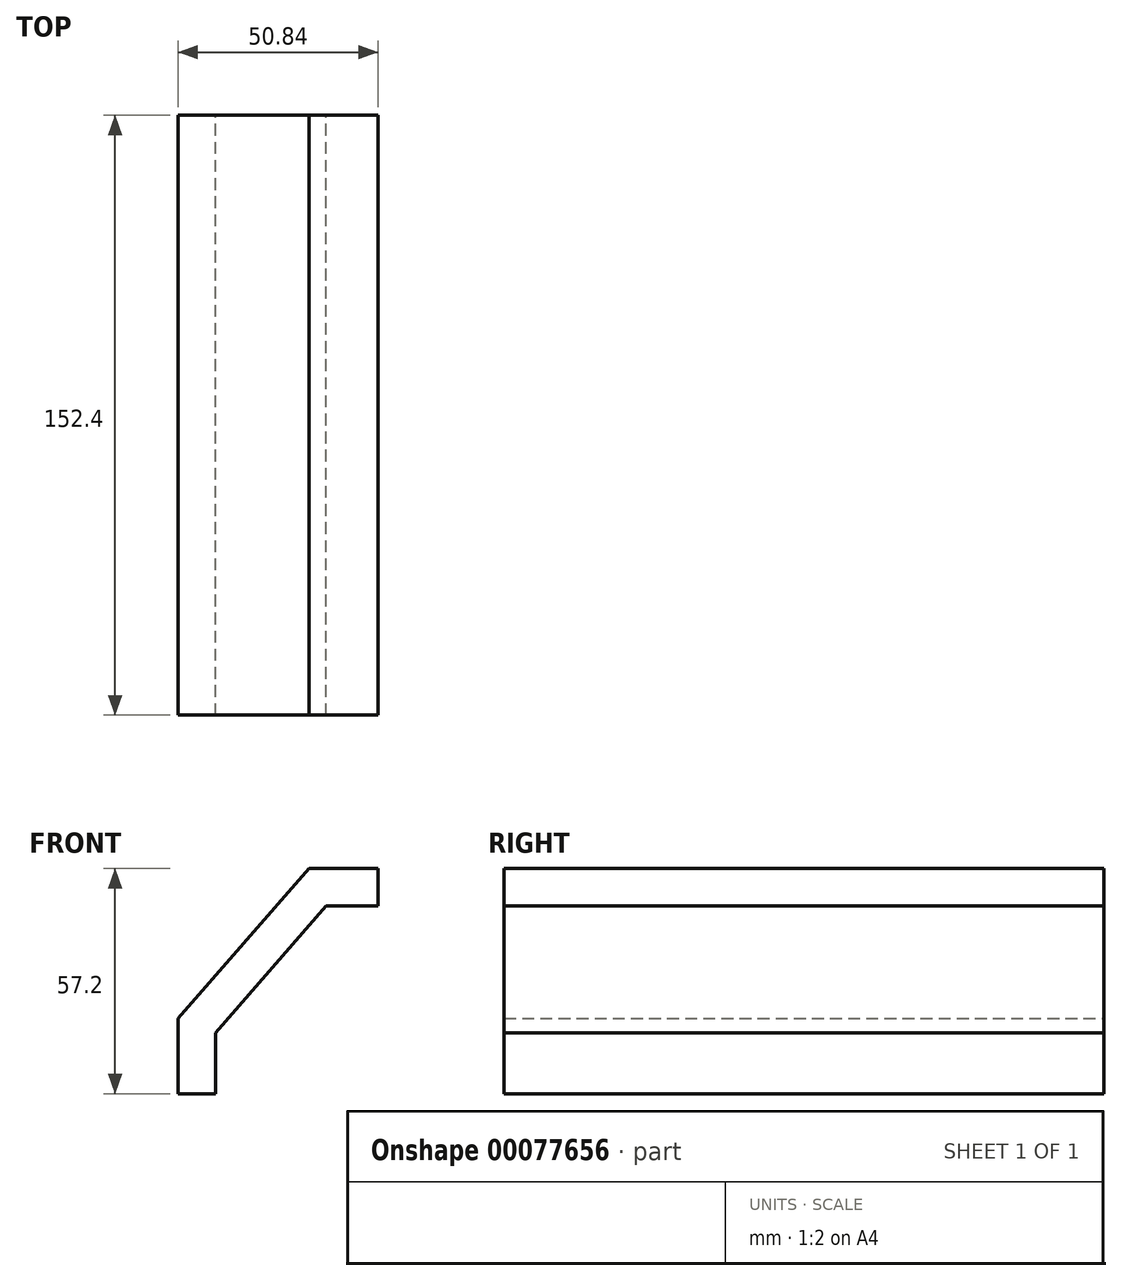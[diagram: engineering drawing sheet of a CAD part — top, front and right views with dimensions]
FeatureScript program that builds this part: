
annotation { "Feature Type Name" : "Feature", "Feature Type Description" : "" }
export const myFeature = defineFeature(function(context is Context, id is Id, definition is map)
    precondition{}
    {
        {
            var Q0;
            Q0=qCreatedBy(makeId("Front.planeOp"),FACE);
            var sketch = newSketch(context, id + "F0", { "sketchPlane" : qUnion([Q0])});
            skLineSegment(sketch, "E0", {"start": v(25.42, 28.6) * mm, "end": v(25.42, 19.06) * mm});
            skLineSegment(sketch, "E1", {"start": v(-25.42, -28.6) * mm, "end": v(-15.89, -28.6) * mm});
            skLineSegment(sketch, "E2", {"start": v(-25.42, -28.6) * mm, "end": v(-25.42, -9.53) * mm});
            skLineSegment(sketch, "E3", {"start": v(-25.42, -9.53) * mm, "end": v(7.87, 28.6) * mm});
            skLineSegment(sketch, "E4", {"start": v(-15.89, -13.1) * mm, "end": v(12.2, 19.06) * mm});
            skLineSegment(sketch, "E5", {"start": v(7.87, 28.6) * mm, "end": v(25.42, 28.6) * mm});
            skLineSegment(sketch, "E6", {"start": v(-15.89, -28.6) * mm, "end": v(-15.89, -13.1) * mm});
            skLineSegment(sketch, "E7", {"start": v(25.42, 19.06) * mm, "end": v(12.2, 19.06) * mm});
            skSolve(sketch);
        }
        {
            var Q0;
            Q0=makeQuery(id+"F0.imprint","IMPRINT",FACE,{"disambiguationData":[TD([[makeQuery(id+"F0.imprint","IMPRINT",EDGE,{"derivedFrom":sQuery(id+"F0.wireOp",EDGE,"E0")}),-1.0]])]});
            extrude(context, id + "F1", {"entities" : qUnion([Q0]), "depth" : 152.4 * mm});
        }
    });
